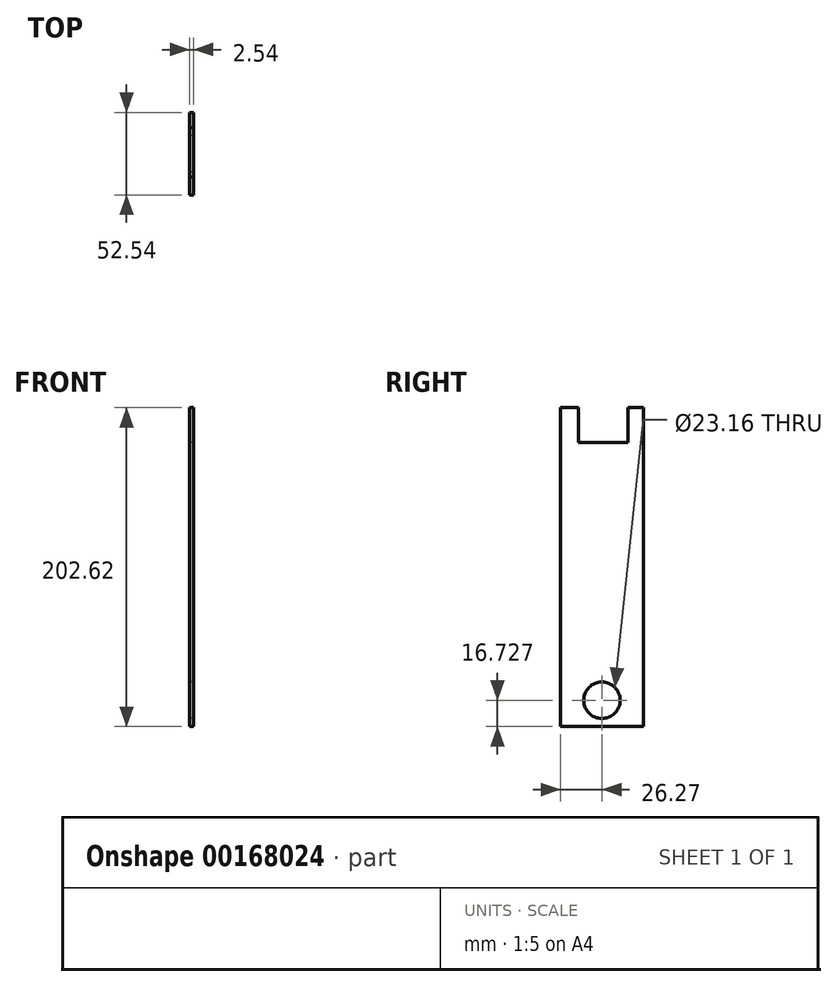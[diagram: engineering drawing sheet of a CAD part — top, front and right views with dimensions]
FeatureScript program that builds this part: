
annotation { "Feature Type Name" : "Feature", "Feature Type Description" : "" }
export const myFeature = defineFeature(function(context is Context, id is Id, definition is map)
    precondition{}
    {
        {
            var Q0;
            Q0=qCreatedBy(makeId("Top.planeOp"),FACE);
            var sketch = newSketch(context, id + "F0", { "sketchPlane" : qUnion([Q0])});
            skLineSegment(sketch, "E0.bottom", {"start": v(25.24, 26.27) * mm, "end": v(-25.24, 26.27) * mm});
            skLineSegment(sketch, "E0.top", {"start": v(25.24, -26.27) * mm, "end": v(-25.24, -26.27) * mm});
            skLineSegment(sketch, "E0.left", {"start": v(25.24, 26.27) * mm, "end": v(25.24, -26.27) * mm});
            skLineSegment(sketch, "E0.right", {"start": v(-25.24, 26.27) * mm, "end": v(-25.24, -26.27) * mm});
            skPoint(sketch, "E0.middle", {"position": v(0, 0) * mm});
            skSolve(sketch);
        }
        {
            var Q0;
            Q0=qSketchRegion(id+"F0",true);
            extrude(context, id + "F1", {"entities" : qUnion([Q0]), "depth" : 128.13 * mm});
        }
        {
            var Q0;
            Q0=makeQuery(id+"F1.opExtrude","CAP_FACE",FACE,{"disambiguationData":[OSD([sQuery(id+"F0.wireOp",EDGE,"E0.bottom"),sQuery(id+"F0.wireOp",EDGE,"E0.top"),sQuery(id+"F0.wireOp",EDGE,"E0.left"),sQuery(id+"F0.wireOp",EDGE,"E0.right")])],"isStart":false});
            shell(context, id + "F2", {"entities" : qUnion([Q0]), "thickness" : 2.54 * mm});
        }
        {
            var Q0;
            Q0=makeQuery(id+"F1.opExtrude","SWEPT_FACE",FACE,{"disambiguationData":[OSD([sQuery(id+"F0.wireOp",EDGE,"E0.top")])]});
            var sketch = newSketch(context, id + "F3", { "sketchPlane" : qUnion([Q0])});
            skEllipse(sketch, "E1", {"center": v(0, 69.47) * mm, "majorRadius": 55.74 * mm, "minorRadius": 4.24 * mm, "majorAxis": v(0, -1)});
            skSolve(sketch);
        }
        {
            var Q0;
            Q0=qSketchRegion(id+"F3",true);
            extrude(context, id + "F4", {"entities" : qUnion([Q0]), "operationType" : NewBodyOperationType.REMOVE, "oppositeDirection" : true, "depth" : 87.94 * mm});
        }
        {
            var Q0;
            Q0=makeQuery(id+"F2.opShell","OFFSET_FACE",FACE,{"disambiguationData":[OSD([sQuery(id+"F0.wireOp",EDGE,"E0.bottom")])]});
            extrude(context, id + "F5", {"entities" : qUnion([Q0]), "operationType" : NewBodyOperationType.REMOVE, "depth" : 92.57 * mm});
        }
        {
            var Q0;
            Q0=makeQuery(id+"F2.opShell","OFFSET_FACE",FACE,{"disambiguationData":[OSD([sQuery(id+"F0.wireOp",EDGE,"E0.bottom")])]});
            extrude(context, id + "F6", {"entities" : qUnion([Q0]), "operationType" : NewBodyOperationType.REMOVE, "oppositeDirection" : true, "depth" : 25.4 * mm});
        }
        {
            var Q0;
            {var subQ0=sQuery(id+"F0.wireOp",EDGE,"E0.bottom");var subQ1=makeQuery(id+"F2.opShell","OFFSET_EDGE",EDGE,{"disambiguationData":[OSD([subQ0]),TDD([makeQuery(id+"F1.opExtrude","CAP_EDGE",EDGE,{"disambiguationData":[OSD([subQ0])],"isStart":true})])]});Q0=makeQuery(id+"F6.boolean.opBoolean","MERGE",FACE,{"derivedFrom":[makeQuery(id+"F5.boolean.opBoolean","MERGE",FACE,{"derivedFrom":[makeQuery(id+"F2.opShell","OFFSET_FACE",FACE,{"disambiguationData":[OSD([subQ0,sQuery(id+"F0.wireOp",EDGE,"E0.top"),sQuery(id+"F0.wireOp",EDGE,"E0.left"),sQuery(id+"F0.wireOp",EDGE,"E0.right")])]}),makeQuery(id+"F5.opExtrude","SWEPT_FACE",FACE,{"disambiguationData":[OSD([subQ0]),TDD([subQ1])]})]}),makeQuery(id+"F6.opExtrude","SWEPT_FACE",FACE,{"disambiguationData":[OSD([subQ0]),TDD([subQ1])]})]});}
            extrude(context, id + "F7", {"entities" : qUnion([Q0]), "operationType" : NewBodyOperationType.REMOVE, "oppositeDirection" : true, "depth" : 25.4 * mm});
        }
        {
            var Q0;
            {var subQ0=sQuery(id+"F0.wireOp",EDGE,"E0.right");var subQ1=sQuery(id+"F0.wireOp",EDGE,"E0.bottom");Q0=makeQuery(id+"F7.boolean.opBoolean","MERGE",FACE,{"derivedFrom":[makeQuery(id+"F6.boolean.opBoolean","MERGE",FACE,{"derivedFrom":[makeQuery(id+"F5.boolean.opBoolean","MERGE",FACE,{"derivedFrom":[makeQuery(id+"F2.opShell","OFFSET_FACE",FACE,{"disambiguationData":[OSD([subQ0])]}),makeQuery(id+"F5.opExtrude","SWEPT_FACE",FACE,{"disambiguationData":[OSD([subQ1,subQ0])]})]}),makeQuery(id+"F6.opExtrude","SWEPT_FACE",FACE,{"disambiguationData":[OSD([subQ1,subQ0])]})]}),makeQuery(id+"F7.opExtrude","SWEPT_FACE",FACE,{"disambiguationData":[OSD([subQ1,subQ0])]})]});}
            extrude(context, id + "F8", {"entities" : qUnion([Q0]), "operationType" : NewBodyOperationType.REMOVE, "oppositeDirection" : true, "depth" : 25.4 * mm});
        }
        {
            var Q0;
            {var subQ0=sQuery(id+"F0.wireOp",EDGE,"E0.left");var subQ1=sQuery(id+"F0.wireOp",EDGE,"E0.top");var subQ2=sQuery(id+"F0.wireOp",EDGE,"E0.bottom");Q0=makeQuery(id+"F6.boolean.opBoolean","SPLIT",FACE,{"disambiguationData":[TD([makeQuery(id+"F1.opExtrude","SWEPT_FACE",FACE,{"disambiguationData":[OSD([subQ0])]})])],"derivedFrom":makeQuery(id+"F1.opExtrude","CAP_FACE",FACE,{"disambiguationData":[OSD([subQ2,subQ1,subQ0,sQuery(id+"F0.wireOp",EDGE,"E0.right")])],"isStart":false})});}
            extrude(context, id + "F9", {"entities" : qUnion([Q0]), "operationType" : NewBodyOperationType.ADD, "depth" : 74.49 * mm});
        }
        {
            var Q0;
            {var subQ0=sQuery(id+"F0.wireOp",EDGE,"E0.left");var subQ1=sQuery(id+"F0.wireOp",EDGE,"E0.bottom");Q0=makeQuery(id+"F9.boolean.opBoolean","MERGE",FACE,{"derivedFrom":[makeQuery(id+"F7.boolean.opBoolean","MERGE",FACE,{"derivedFrom":[makeQuery(id+"F6.boolean.opBoolean","MERGE",FACE,{"derivedFrom":[makeQuery(id+"F5.boolean.opBoolean","MERGE",FACE,{"derivedFrom":[makeQuery(id+"F2.opShell","OFFSET_FACE",FACE,{"disambiguationData":[OSD([subQ0])]}),makeQuery(id+"F5.opExtrude","SWEPT_FACE",FACE,{"disambiguationData":[OSD([subQ1,subQ0])]})]}),makeQuery(id+"F6.opExtrude","SWEPT_FACE",FACE,{"disambiguationData":[OSD([subQ1,subQ0])]})]}),makeQuery(id+"F7.opExtrude","SWEPT_FACE",FACE,{"disambiguationData":[OSD([subQ1,subQ0])]})]}),makeQuery(id+"F9.opExtrude","SWEPT_FACE",FACE,{"disambiguationData":[OSD([subQ1,subQ0])]})]});}
            var sketch = newSketch(context, id + "F10", { "sketchPlane" : qUnion([Q0])});
            skLineSegment(sketch, "E2", {"start": v(-16.5, 202.62) * mm, "end": v(-16.5, 180.49) * mm});
            skLineSegment(sketch, "E3", {"start": v(-16.5, 180.49) * mm, "end": v(14.96, 180.49) * mm});
            skLineSegment(sketch, "E4", {"start": v(14.96, 180.49) * mm, "end": v(14.96, 202.62) * mm});
            skLineSegment(sketch, "E5", {"start": v(14.96, 202.62) * mm, "end": v(-16.5, 202.62) * mm});
            skSolve(sketch);
        }
        {
            var Q0;
            Q0 = qSketchRegion(id + "F10", true);
            extrude(context, id + "F11", {"entities" : qUnion([Q0]), "operationType" : NewBodyOperationType.REMOVE, "oppositeDirection" : true, "depth" : 25.4 * mm});
        }
        {
            var Q0;
            {var subQ0=sQuery(id+"F0.wireOp",EDGE,"E0.left");var subQ1=sQuery(id+"F0.wireOp",EDGE,"E0.bottom");Q0=makeQuery(id+"F9.boolean.opBoolean","MERGE",FACE,{"derivedFrom":[makeQuery(id+"F7.boolean.opBoolean","MERGE",FACE,{"derivedFrom":[makeQuery(id+"F6.boolean.opBoolean","MERGE",FACE,{"derivedFrom":[makeQuery(id+"F5.boolean.opBoolean","MERGE",FACE,{"derivedFrom":[makeQuery(id+"F2.opShell","OFFSET_FACE",FACE,{"disambiguationData":[OSD([subQ0])]}),makeQuery(id+"F5.opExtrude","SWEPT_FACE",FACE,{"disambiguationData":[OSD([subQ1,subQ0])]})]}),makeQuery(id+"F6.opExtrude","SWEPT_FACE",FACE,{"disambiguationData":[OSD([subQ1,subQ0])]})]}),makeQuery(id+"F7.opExtrude","SWEPT_FACE",FACE,{"disambiguationData":[OSD([subQ1,subQ0])]})]}),makeQuery(id+"F9.opExtrude","SWEPT_FACE",FACE,{"disambiguationData":[OSD([subQ1,subQ0])]})]});}
            var sketch = newSketch(context, id + "F12", { "sketchPlane" : qUnion([Q0])});
            skCircle(sketch, "E6", {"center": v(0, 16.73) * mm, "radius": 11.58 * mm});
            skSolve(sketch);
        }
        {
            var Q0;
            Q0 = qSketchRegion(id + "F12", true);
            extrude(context, id + "F13", {"entities" : qUnion([Q0]), "operationType" : NewBodyOperationType.REMOVE, "oppositeDirection" : true, "depth" : 25.4 * mm});
        }
    });
